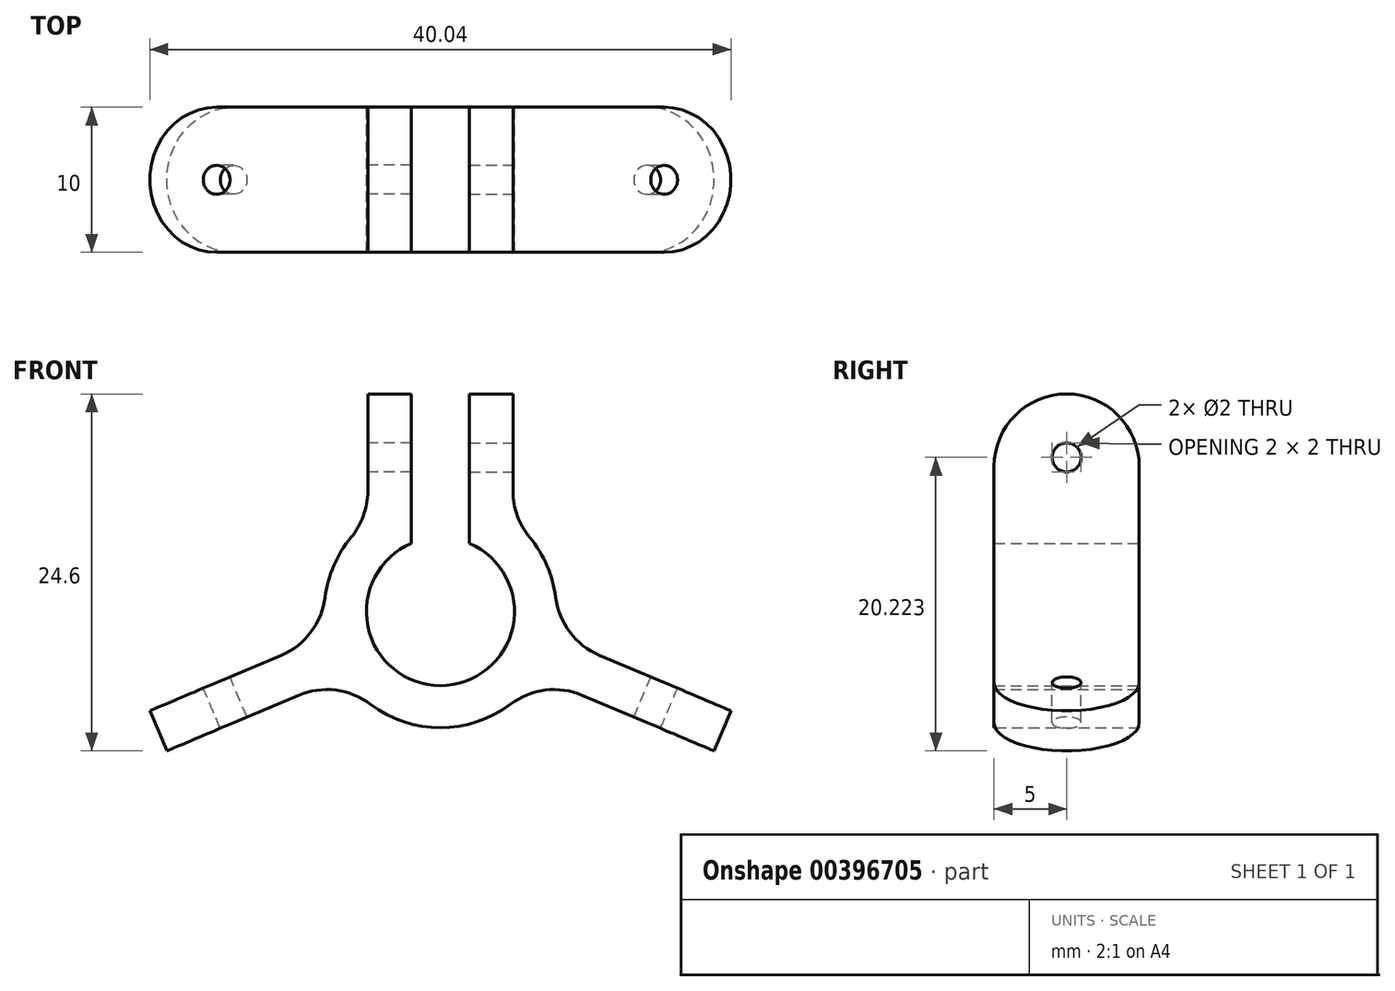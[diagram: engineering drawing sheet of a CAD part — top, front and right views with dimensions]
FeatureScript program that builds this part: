
annotation { "Feature Type Name" : "Feature", "Feature Type Description" : "" }
export const myFeature = defineFeature(function(context is Context, id is Id, definition is map)
    precondition{}
    {
        {
            var Q0;
            Q0=qCreatedBy(makeId("Front.planeOp"),FACE);
            var sketch = newSketch(context, id + "F0", { "sketchPlane" : qUnion([Q0])});
            skArc(sketch, "E0", {"start": v(0, -5.1) * mm, "mid": v(5, -1.02) * mm, "end": v(2, 4.7) * mm});
            skLineSegment(sketch, "E1", {"start": v(0, 0) * mm, "end": v(24.3, -10.28) * mm, "construction": true});
            skLineSegment(sketch, "E2", {"start": v(3.9, -3.28) * mm, "end": v(18.85, -9.6) * mm});
            skLineSegment(sketch, "E3", {"start": v(18.85, -9.6) * mm, "end": v(20.02, -6.84) * mm});
            skLineSegment(sketch, "E4", {"start": v(20.02, -6.84) * mm, "end": v(5.07, -0.52) * mm});
            skLineSegment(sketch, "E5", {"start": v(5, 15) * mm, "end": v(5, 6.24) * mm});
            skLineSegment(sketch, "E6", {"start": v(2, 4.7) * mm, "end": v(2, 15) * mm});
            skLineSegment(sketch, "E7.trimOffspring", {"start": v(2, 15) * mm, "end": v(5, 15) * mm});
            skLineSegment(sketch, "E8", {"start": v(0, 15) * mm, "end": v(0, -19.29) * mm, "construction": true});
            skArc(sketch, "E9.trimOffspring", {"start": v(0, -8) * mm, "mid": v(7.94, -1) * mm, "end": v(2, 7.75) * mm});
            skLineSegment(sketch, "E10", {"start": v(0, -5.1) * mm, "end": v(0, -8) * mm});
            skSolve(sketch);
        }
        {
            var Q0;
            {var subQ4=sQuery(id+"F0.wireOp",EDGE,"E6");var subQ6=sQuery(id+"F0.wireOp",EDGE,"E0");var subQ8=makeQuery(id+"F0.imprint","INTERSECT",VERTEX,{"derivedFrom":[subQ6,subQ4]});Q0=makeQuery(id+"F0.imprint","IMPRINT",FACE,{"disambiguationData":[TD([[makeQuery(id+"F0.imprint","IMPRINT",EDGE,{"disambiguationData":[TD([[subQ8,1.0]])],"derivedFrom":subQ6}),-1.0]])]});}
            var Q1;
            {var subQ0=sQuery(id+"F0.wireOp",EDGE,"E2");var subQ1=sQuery(id+"F0.wireOp",EDGE,"E0");var subQ2=makeQuery(id+"F0.imprint","INTERSECT",VERTEX,{"derivedFrom":[subQ1,subQ0]});Q1=makeQuery(id+"F0.imprint","IMPRINT",FACE,{"disambiguationData":[TD([[makeQuery(id+"F0.imprint","IMPRINT",EDGE,{"disambiguationData":[TD([[subQ2,-1.0]])],"derivedFrom":subQ1}),-1.0]])]});}
            var Q2;
            {var subQ4=sQuery(id+"F0.wireOp",EDGE,"i9qYtkfv-SZLV-WTxb-UqVO-jSNCvkcmy04q");var subQ6=sQuery(id+"F0.wireOp",EDGE,"E0");var subQ8=makeQuery(id+"F0.imprint","INTERSECT",VERTEX,{"derivedFrom":[subQ6,subQ4]});Q2=makeQuery(id+"F0.imprint","IMPRINT",FACE,{"disambiguationData":[TD([[makeQuery(id+"F0.imprint","IMPRINT",EDGE,{"disambiguationData":[TD([[subQ8,-1.0]])],"derivedFrom":subQ6}),-1.0]])]});}
            var Q3;
            {var subQ3=sQuery(id+"F0.wireOp",EDGE,"g51z1Yhh-3KAa-QBzB-FuLV-YnATeuSFtZAR");Q3=makeQuery(id+"F0.imprint","IMPRINT",FACE,{"disambiguationData":[TD([[makeQuery(id+"F0.imprint","IMPRINT",EDGE,{"derivedFrom":subQ3}),-1.0]])]});}
            var Q4;
            {var subQ3=sQuery(id+"F0.wireOp",EDGE,"E5");Q4=makeQuery(id+"F0.imprint","IMPRINT",FACE,{"disambiguationData":[TD([[makeQuery(id+"F0.imprint","IMPRINT",EDGE,{"derivedFrom":subQ3}),-1.0]])]});}
            var Q5;
            {var subQ0=sQuery(id+"F0.wireOp",EDGE,"E3");Q5=makeQuery(id+"F0.imprint","IMPRINT",FACE,{"disambiguationData":[TD([[makeQuery(id+"F0.imprint","IMPRINT",EDGE,{"derivedFrom":subQ0}),1.0]])]});}
            extrude(context, id + "F1", {"entities" : qUnion([Q0, Q1, Q2, Q3, Q4, Q5]), "endBound" : BoundingType.SYMMETRIC, "depth" : 10 * mm});
        }
        {
            var Q0;
            Q0=makeQuery(id+"F1.opExtrude","SWEPT_FACE",FACE,{"disambiguationData":[OSD([sQuery(id+"F0.wireOp",EDGE,"E4")])]});
            var sketch = newSketch(context, id + "F2", { "sketchPlane" : qUnion([Q0])});
            skLineSegment(sketch, "E11", {"start": v(16.1, -5) * mm, "end": v(16.1, 5) * mm, "construction": true});
            skCircle(sketch, "E12", {"center": v(16.1, 0) * mm, "radius": 1 * mm});
            skSolve(sketch);
        }
        {
            var Q0;
            Q0=makeQuery(id+"F2.imprint","IMPRINT",FACE,{"disambiguationData":[TD([[makeQuery(id+"F2.imprint","IMPRINT",EDGE,{"derivedFrom":sQuery(id+"F2.wireOp",EDGE,"E12")}),1.0]])]});
            extrude(context, id + "F3", {"entities" : qUnion([Q0]), "operationType" : NewBodyOperationType.REMOVE, "oppositeDirection" : true, "depth" : 25 * mm});
        }
        {
            var Q0;
            Q0=makeQuery(id+"F1.opExtrude","SWEPT_FACE",FACE,{"disambiguationData":[OSD([sQuery(id+"F0.wireOp",EDGE,"E5")])]});
            var sketch = newSketch(context, id + "F4", { "sketchPlane" : qUnion([Q0])});
            skLineSegment(sketch, "E13", {"start": v(-5, 10.62) * mm, "end": v(5, 10.62) * mm, "construction": true});
            skLineSegment(sketch, "E14", {"start": v(0, 15) * mm, "end": v(0, 6.24) * mm, "construction": true});
            skCircle(sketch, "E15", {"center": v(0, 10.62) * mm, "radius": 1 * mm});
            skSolve(sketch);
        }
        {
            var Q0;
            Q0 = qSketchRegion(id + "F4", true);
            extrude(context, id + "F5", {"entities" : qUnion([Q0]), "operationType" : NewBodyOperationType.REMOVE, "oppositeDirection" : true, "depth" : 25 * mm});
        }
        {
            var Q0;
            Q0=makeQuery(id+"F1.opExtrude","CAP_EDGE",EDGE,{"disambiguationData":[OSD([sQuery(id+"F0.wireOp",EDGE,"E3")])],"isStart":true});
            var Q1;
            Q1=makeQuery(id+"F1.opExtrude","CAP_EDGE",EDGE,{"disambiguationData":[OSD([sQuery(id+"F0.wireOp",EDGE,"E3")])],"isStart":false});
            var Q2;
            Q2=makeQuery(id+"F1.opExtrude","CAP_EDGE",EDGE,{"disambiguationData":[OSD([sQuery(id+"F0.wireOp",EDGE,"E7.trimOffspring")])],"isStart":false});
            var Q3;
            Q3=makeQuery(id+"F1.opExtrude","CAP_EDGE",EDGE,{"disambiguationData":[OSD([sQuery(id+"F0.wireOp",EDGE,"E7.trimOffspring")])],"isStart":true});
            fillet(context, id + "F6", {"entities" : qUnion([Q0, Q1, Q2, Q3]), "radius" : 5 * mm, "tangentPropagation" : true, "allowEdgeOverflow" : false});
        }
        {
            var Q0;
            Q0=makeQuery(id+"F1.opExtrude","SWEPT_EDGE",EDGE,{"disambiguationData":[OSD([sQuery(id+"F0.wireOp",EDGE,"E5"),sQuery(id+"F0.wireOp",EDGE,"E9.trimOffspring")])]});
            var Q1;
            Q1=makeQuery(id+"F1.opExtrude","SWEPT_EDGE",EDGE,{"disambiguationData":[OSD([sQuery(id+"F0.wireOp",EDGE,"E4"),sQuery(id+"F0.wireOp",EDGE,"E9.trimOffspring")])]});
            var Q2;
            Q2=makeQuery(id+"F1.opExtrude","SWEPT_EDGE",EDGE,{"disambiguationData":[OSD([sQuery(id+"F0.wireOp",EDGE,"E2"),sQuery(id+"F0.wireOp",EDGE,"E9.trimOffspring")])]});
            fillet(context, id + "F7", {"entities" : qUnion([Q0, Q1, Q2]), "radius" : 5 * mm, "tangentPropagation" : true, "allowEdgeOverflow" : false});
        }
        {
            var Q0;
            Q0=makeQuery(id+"F1.opExtrude","SWEPT_BODY",BODY,{"disambiguationData":[OSD([sQuery(id+"F0.wireOp",EDGE,"E0"),sQuery(id+"F0.wireOp",EDGE,"E2"),sQuery(id+"F0.wireOp",EDGE,"E3"),sQuery(id+"F0.wireOp",EDGE,"E4"),sQuery(id+"F0.wireOp",EDGE,"E5"),sQuery(id+"F0.wireOp",EDGE,"E6"),sQuery(id+"F0.wireOp",EDGE,"E7.trimOffspring"),sQuery(id+"F0.wireOp",EDGE,"E9.trimOffspring"),sQuery(id+"F0.wireOp",EDGE,"E10")])]});
            var Q1;
            Q1=qCreatedBy(makeId("Right.planeOp"),FACE);
            mirror(context, id + "F8", {"operationType" : NewBodyOperationType.ADD, "entities" : qUnion([Q0]), "mirrorPlane" : qUnion([Q1])});
        }
    });
